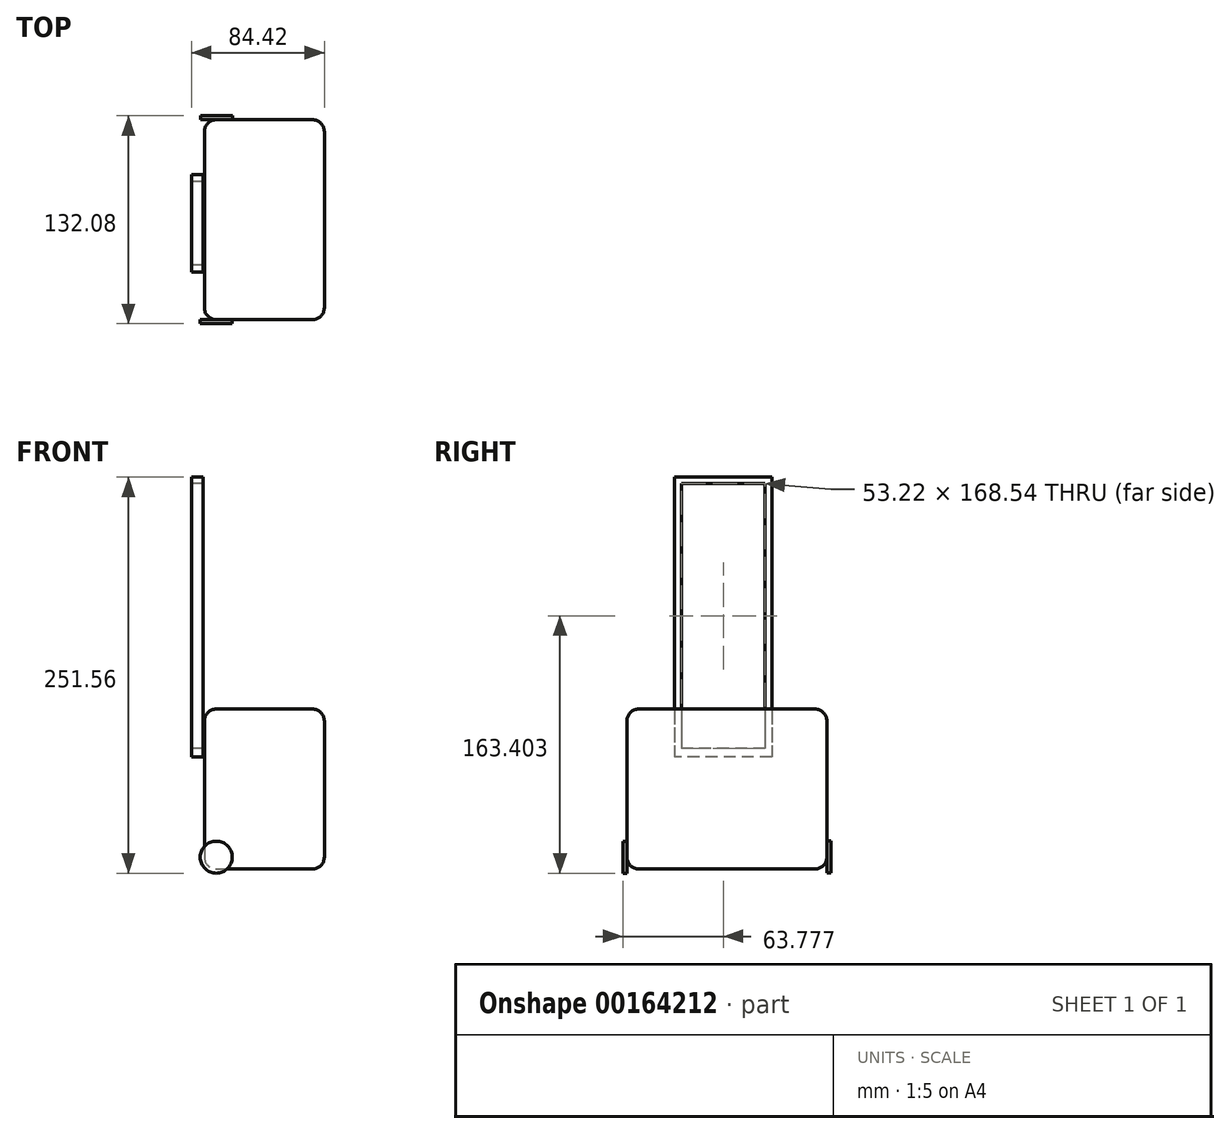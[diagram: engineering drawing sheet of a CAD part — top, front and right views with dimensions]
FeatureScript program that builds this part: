
annotation { "Feature Type Name" : "Feature", "Feature Type Description" : "" }
export const myFeature = defineFeature(function(context is Context, id is Id, definition is map)
    precondition{}
    {
        {
            var Q0;
            Q0=qCreatedBy(makeId("Front.planeOp"),FACE);
            var sketch = newSketch(context, id + "F0", { "sketchPlane" : qUnion([Q0])});
            skLineSegment(sketch, "E0.bottom", {"start": v(-45.55, 46.82) * mm, "end": v(30.65, 46.82) * mm});
            skLineSegment(sketch, "E0.top", {"start": v(-45.55, -54.78) * mm, "end": v(30.65, -54.78) * mm});
            skLineSegment(sketch, "E0.left", {"start": v(-45.55, 46.82) * mm, "end": v(-45.55, -54.78) * mm});
            skLineSegment(sketch, "E0.right", {"start": v(30.65, 46.82) * mm, "end": v(30.65, -54.78) * mm});
            skSolve(sketch);
        }
        {
            var Q0;
            Q0=makeQuery(id+"F0.imprint","IMPRINT",FACE,{"disambiguationData":[TD([[makeQuery(id+"F0.imprint","IMPRINT",EDGE,{"derivedFrom":sQuery(id+"F0.wireOp",EDGE,"E0.bottom")}),-1.0]])]});
            extrude(context, id + "F1", {"entities" : qUnion([Q0]), "depth" : 127 * mm});
        }
        {
            var Q0;
            Q0=makeQuery(id+"F1.opExtrude","CAP_EDGE",EDGE,{"disambiguationData":[OSD([sQuery(id+"F0.wireOp",EDGE,"E0.bottom")])],"isStart":false});
            var Q1;
            Q1=makeQuery(id+"F1.opExtrude","SWEPT_EDGE",EDGE,{"disambiguationData":[OSD([sQuery(id+"F0.wireOp",EDGE,"E0.bottom"),sQuery(id+"F0.wireOp",EDGE,"E0.right")])]});
            var Q2;
            Q2=makeQuery(id+"F1.opExtrude","CAP_EDGE",EDGE,{"disambiguationData":[OSD([sQuery(id+"F0.wireOp",EDGE,"E0.bottom")])],"isStart":true});
            var Q3;
            Q3=makeQuery(id+"F1.opExtrude","SWEPT_EDGE",EDGE,{"disambiguationData":[OSD([sQuery(id+"F0.wireOp",EDGE,"E0.bottom"),sQuery(id+"F0.wireOp",EDGE,"E0.left")])]});
            var Q4;
            Q4=makeQuery(id+"F1.opExtrude","CAP_EDGE",EDGE,{"disambiguationData":[OSD([sQuery(id+"F0.wireOp",EDGE,"E0.left")])],"isStart":false});
            var Q5;
            Q5=makeQuery(id+"F1.opExtrude","CAP_EDGE",EDGE,{"disambiguationData":[OSD([sQuery(id+"F0.wireOp",EDGE,"E0.right")])],"isStart":false});
            var Q6;
            Q6=makeQuery(id+"F1.opExtrude","CAP_EDGE",EDGE,{"disambiguationData":[OSD([sQuery(id+"F0.wireOp",EDGE,"E0.right")])],"isStart":true});
            var Q7;
            Q7=makeQuery(id+"F1.opExtrude","SWEPT_EDGE",EDGE,{"disambiguationData":[OSD([sQuery(id+"F0.wireOp",EDGE,"E0.top"),sQuery(id+"F0.wireOp",EDGE,"E0.right")])]});
            var Q8;
            Q8=makeQuery(id+"F1.opExtrude","CAP_EDGE",EDGE,{"disambiguationData":[OSD([sQuery(id+"F0.wireOp",EDGE,"E0.top")])],"isStart":false});
            var Q9;
            Q9=makeQuery(id+"F1.opExtrude","CAP_EDGE",EDGE,{"disambiguationData":[OSD([sQuery(id+"F0.wireOp",EDGE,"E0.left")])],"isStart":true});
            var Q10;
            Q10=makeQuery(id+"F1.opExtrude","SWEPT_EDGE",EDGE,{"disambiguationData":[OSD([sQuery(id+"F0.wireOp",EDGE,"E0.top"),sQuery(id+"F0.wireOp",EDGE,"E0.left")])]});
            var Q11;
            Q11=makeQuery(id+"F1.opExtrude","CAP_EDGE",EDGE,{"disambiguationData":[OSD([sQuery(id+"F0.wireOp",EDGE,"E0.top")])],"isStart":true});
            fillet(context, id + "F2", {"entities" : qUnion([Q0, Q1, Q2, Q3, Q4, Q5, Q6, Q7, Q8, Q9, Q10, Q11]), "radius" : 7.62 * mm, "tangentPropagation" : true, "allowEdgeOverflow" : false});
        }
        {
            var Q0;
            Q0=makeQuery(id+"F1.opExtrude","CAP_FACE",FACE,{"disambiguationData":[OSD([sQuery(id+"F0.wireOp",EDGE,"E0.bottom"),sQuery(id+"F0.wireOp",EDGE,"E0.top"),sQuery(id+"F0.wireOp",EDGE,"E0.left"),sQuery(id+"F0.wireOp",EDGE,"E0.right")])],"isStart":false});
            cPlane(context, id + "F3", {"entities" : qUnion([Q0]), "cplaneType" : CPlaneType.OFFSET, "offset" : 2.54 * mm, "width" : 152.4 * mm, "height" : 152.4 * mm});
        }
        {
            var Q0;
            Q0=qCreatedBy(id+"F3.planeOp",FACE);
            var sketch = newSketch(context, id + "F4", { "sketchPlane" : qUnion([Q0])});
            skCircle(sketch, "E1", {"center": v(-38, -47.26) * mm, "radius": 10.16 * mm});
            skSolve(sketch);
        }
        {
            var Q0;
            Q0 = qSketchRegion(id + "F4", true);
            extrude(context, id + "F5", {"entities" : qUnion([Q0]), "oppositeDirection" : true, "depth" : 2.54 * mm});
        }
        {
            var Q0;
            Q0=makeQuery(id+"F1.opExtrude","CAP_FACE",FACE,{"disambiguationData":[OSD([sQuery(id+"F0.wireOp",EDGE,"E0.bottom"),sQuery(id+"F0.wireOp",EDGE,"E0.top"),sQuery(id+"F0.wireOp",EDGE,"E0.left"),sQuery(id+"F0.wireOp",EDGE,"E0.right")])],"isStart":true});
            cPlane(context, id + "F6", {"entities" : qUnion([Q0]), "cplaneType" : CPlaneType.OFFSET, "offset" : 2.54 * mm, "width" : 152.4 * mm, "height" : 152.4 * mm});
        }
        {
            var Q0;
            Q0=qCreatedBy(id+"F6.planeOp",FACE);
            var sketch = newSketch(context, id + "F7", { "sketchPlane" : qUnion([Q0])});
            skCircle(sketch, "E2", {"center": v(37.75, -47) * mm, "radius": 10.16 * mm});
            skSolve(sketch);
        }
        {
            var Q0;
            Q0 = qSketchRegion(id + "F7", true);
            extrude(context, id + "F8", {"entities" : qUnion([Q0]), "oppositeDirection" : true, "depth" : 2.54 * mm});
        }
        {
            var Q0;
            Q0=makeQuery(id+"F1.opExtrude","SWEPT_FACE",FACE,{"disambiguationData":[OSD([sQuery(id+"F0.wireOp",EDGE,"E0.bottom")])]});
            cPlane(context, id + "F9", {"entities" : qUnion([Q0]), "cplaneType" : CPlaneType.OFFSET, "offset" : 30.48 * mm, "oppositeDirection" : true, "width" : 152.4 * mm, "height" : 152.4 * mm});
        }
        {
            var Q0;
            Q0=qCreatedBy(id+"F9.planeOp",FACE);
            var sketch = newSketch(context, id + "F10", { "sketchPlane" : qUnion([Q0])});
            skLineSegment(sketch, "E3.bottom", {"start": v(-46.23, -34.94) * mm, "end": v(-53.77, -34.94) * mm});
            skLineSegment(sketch, "E3.top", {"start": v(-46.23, -96.77) * mm, "end": v(-53.77, -96.77) * mm});
            skLineSegment(sketch, "E3.left", {"start": v(-46.23, -34.94) * mm, "end": v(-46.23, -96.77) * mm});
            skLineSegment(sketch, "E3.right", {"start": v(-53.77, -34.94) * mm, "end": v(-53.77, -96.77) * mm});
            skSolve(sketch);
        }
        {
            var Q0;
            Q0 = qSketchRegion(id + "F10", true);
            extrude(context, id + "F11", {"entities" : qUnion([Q0]), "depth" : 177.8 * mm});
        }
        {
            var Q0;
            Q0=makeQuery(id+"F11.opExtrude","SWEPT_FACE",FACE,{"disambiguationData":[OSD([sQuery(id+"F10.wireOp",EDGE,"E3.right")])]});
            var sketch = newSketch(context, id + "F12", { "sketchPlane" : qUnion([Q0])});
            skLineSegment(sketch, "E4.bottom", {"start": v(39.15, 190.25) * mm, "end": v(92.37, 190.25) * mm});
            skLineSegment(sketch, "E4.top", {"start": v(39.15, 21.71) * mm, "end": v(92.37, 21.71) * mm});
            skLineSegment(sketch, "E4.left", {"start": v(39.15, 190.25) * mm, "end": v(39.15, 21.71) * mm});
            skLineSegment(sketch, "E4.right", {"start": v(92.37, 190.25) * mm, "end": v(92.37, 21.71) * mm});
            skSolve(sketch);
        }
        {
            var Q0;
            Q0=makeQuery(id+"F12.imprint","IMPRINT",FACE,{"disambiguationData":[TD([[makeQuery(id+"F12.imprint","IMPRINT",EDGE,{"derivedFrom":sQuery(id+"F12.wireOp",EDGE,"E4.bottom")}),-1.0]])]});
            extrude(context, id + "F13", {"entities" : qUnion([Q0]), "operationType" : NewBodyOperationType.REMOVE, "endBound" : BoundingType.UP_TO_NEXT, "oppositeDirection" : true, "depth" : 25.4 * mm});
        }
    });
